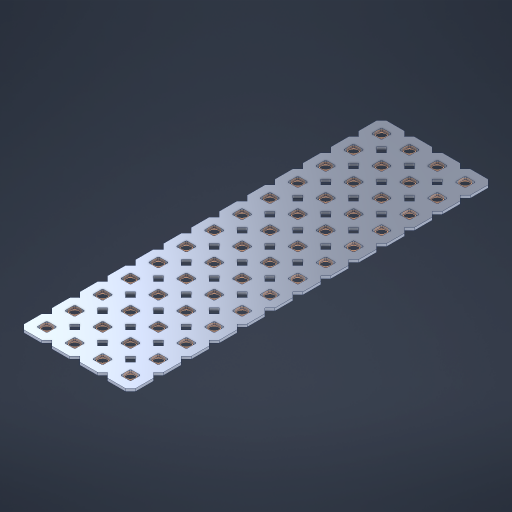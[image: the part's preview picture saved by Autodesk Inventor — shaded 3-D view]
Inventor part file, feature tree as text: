
AUTODESK INVENTOR PART (.ipt)
format: ipt  version: 2023 (Build 270158000, 158)  size: 862,720 bytes
history: native  units: in
note: dims shown in document units (in); Inventor stores cm internally (conversion verified against a paired STEP export)
features: other x53, extrude x51, sketch x2, pattern_linear x1
ambient origin geometry x8: Origin, YZ Plane, XZ Plane, XY Plane, X Axis, Y Axis, Z Axis, Center Point
bodies: Solid1 (feature_tree), Body (feature_tree)
feature tree (107):
  pattern_linear  "Rectangular Pattern1"  Spacing1=0.09in  [1 undecoded]
  sketch  "Sketch1"  dims[d1=0.5in]
  sketch  "Sketch2"  dims[d2=0.182in d3=0.09in d4=0.09in d5=0.09in d6=0.09in d7=0.09in d8=0.09in d9=0.09in d10=0.09in d11=0.02in d13=0.0in d14=0.172in d15=0.0625in d16=0.0in d19=0.5in d22=0.5in]
  other  "Srf1"
  other  "Srf126"
  other  "Srf127"
  other  "Srf128"
  other  "Srf129"
  other  "Srf130"
  other  "Srf131"
  other  "Srf250"
  other  "Srf251"
  other  "Srf252"
  other  "Srf253"
  other  "Srf254"
  other  "Srf255"
  other  "Srf268"
  other  "Srf269"
  other  "Srf270"
  other  "Srf271"
  other  "Srf272"
  other  "Srf273"
  other  "Srf274"
  other  "Srf275"
  other  "Srf276"
  other  "Srf277"
  other  "Srf278"
  other  "Srf279"
  other  "Srf280"
  other  "Srf293"
  other  "Srf294"
  other  "Srf295"
  other  "Srf296"
  other  "Srf297"
  other  "Srf298"
  other  "Srf299"
  other  "Srf300"
  other  "Srf301"
  other  "Srf302"
  other  "Srf303"
  other  "Srf304"
  other  "Srf305"
  other  "Srf318"
  other  "Srf319"
  other  "Srf320"
  other  "Srf321"
  other  "Srf322"
  other  "Srf323"
  other  "Srf324"
  other  "Srf325"
  other  "Srf326"
  other  "Srf327"
  other  "Srf328"
  other  "Srf329"
  other  "Srf330"
  other  "Circle"
  extrude  "ExtrusionSrf126"  Depth=0.09in
  extrude  "ExtrusionSrf127"  Depth=0.09in
  extrude  "ExtrusionSrf128"  Depth=0.09in
  extrude  "ExtrusionSrf129"  Depth=0.09in
  extrude  "ExtrusionSrf130"  Depth=0.09in
  extrude  "ExtrusionSrf131"  Depth=0.09in
  extrude  "ExtrusionSrf250"  Depth=0.09in
  extrude  "ExtrusionSrf251"  Depth=0.02in
  extrude  "ExtrusionSrf252"  TaperAngle=0.0deg  [1 undecoded]
  extrude  "ExtrusionSrf253"  Depth=0.5in
  extrude  "ExtrusionSrf254"  Depth=0.5in TaperAngle=0.0deg
  extrude  "ExtrusionSrf255"  Depth=0.5in
  extrude  "ExtrusionSrf268"  Depth=0.5in
  extrude  "ExtrusionSrf269"  [1 undecoded]
  extrude  "ExtrusionSrf270"  [1 undecoded]
  extrude  "ExtrusionSrf271"  [1 undecoded]
  extrude  "ExtrusionSrf272"  [1 undecoded]
  extrude  "ExtrusionSrf273"  [1 undecoded]
  extrude  "ExtrusionSrf274"  [1 undecoded]
  extrude  "ExtrusionSrf275"  [1 undecoded]
  extrude  "ExtrusionSrf276"  [1 undecoded]
  extrude  "ExtrusionSrf277"  [1 undecoded]
  extrude  "ExtrusionSrf278"  [1 undecoded]
  extrude  "ExtrusionSrf279"  [1 undecoded]
  extrude  "ExtrusionSrf280"  [1 undecoded]
  extrude  "ExtrusionSrf293"  [1 undecoded]
  extrude  "ExtrusionSrf294"  [1 undecoded]
  extrude  "ExtrusionSrf295"  [1 undecoded]
  extrude  "ExtrusionSrf296"  [1 undecoded]
  extrude  "ExtrusionSrf297"  [1 undecoded]
  extrude  "ExtrusionSrf298"  [1 undecoded]
  extrude  "ExtrusionSrf299"  [1 undecoded]
  extrude  "ExtrusionSrf300"  [1 undecoded]
  extrude  "ExtrusionSrf301"  [1 undecoded]
  extrude  "ExtrusionSrf302"  [1 undecoded]
  extrude  "ExtrusionSrf303"  [1 undecoded]
  extrude  "ExtrusionSrf304"  [1 undecoded]
  extrude  "ExtrusionSrf305"  [1 undecoded]
  extrude  "ExtrusionSrf318"  [1 undecoded]
  extrude  "ExtrusionSrf319"  [1 undecoded]
  extrude  "ExtrusionSrf320"  [1 undecoded]
  extrude  "ExtrusionSrf321"  [1 undecoded]
  extrude  "ExtrusionSrf322"  [1 undecoded]
  extrude  "ExtrusionSrf323"  [1 undecoded]
  extrude  "ExtrusionSrf324"  [1 undecoded]
  extrude  "ExtrusionSrf325"  [1 undecoded]
  extrude  "ExtrusionSrf326"  [1 undecoded]
  extrude  "ExtrusionSrf327"  [1 undecoded]
  extrude  "ExtrusionSrf328"  [1 undecoded]
  extrude  "ExtrusionSrf329"  [1 undecoded]
  extrude  "ExtrusionSrf330"  [1 undecoded]
note: 40 required parameter values undecoded (feature->parameter linkage not recoverable at this tier; creation-order binding heuristic only, values carry confidence <= 0.55)
